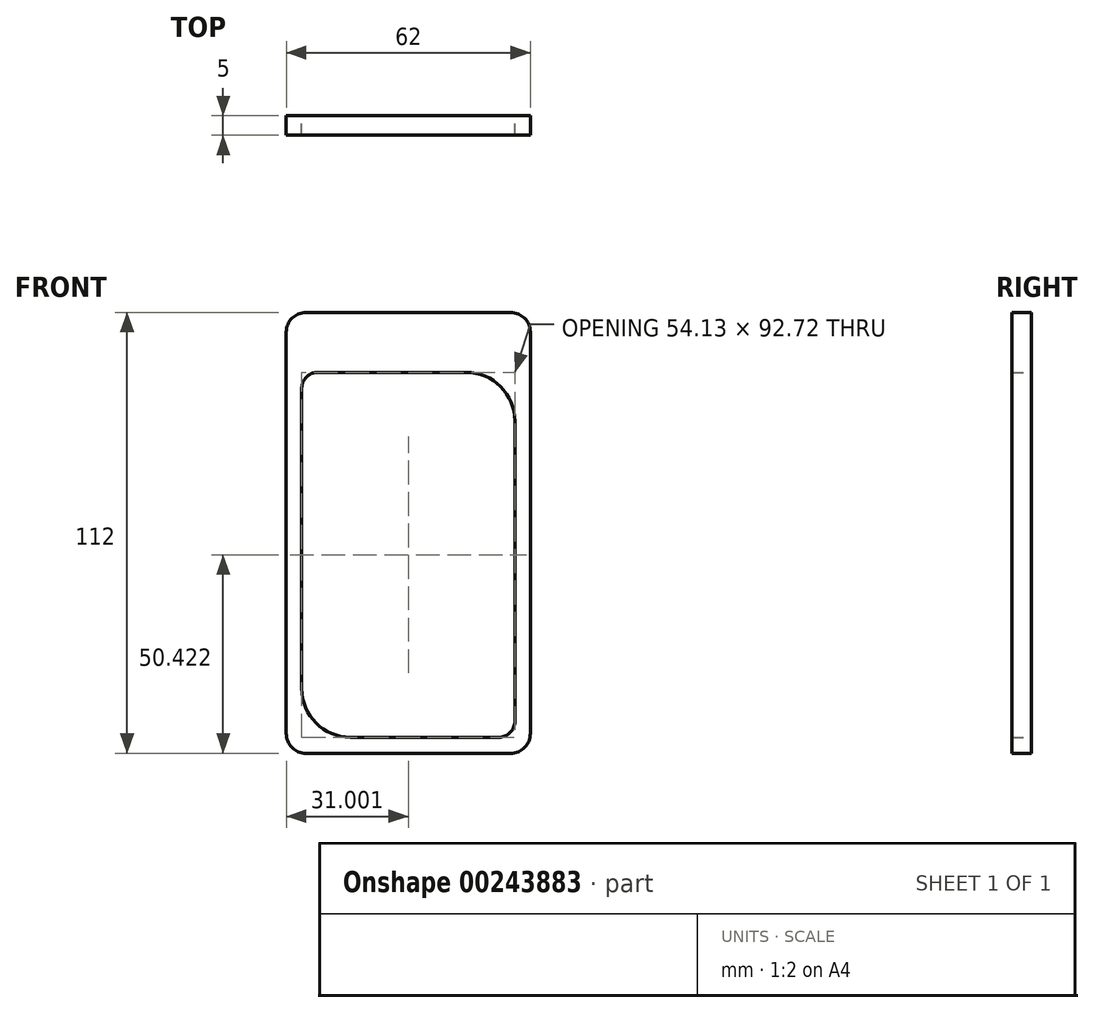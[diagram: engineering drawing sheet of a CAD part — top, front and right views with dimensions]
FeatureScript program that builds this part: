
annotation { "Feature Type Name" : "Feature", "Feature Type Description" : "" }
export const myFeature = defineFeature(function(context is Context, id is Id, definition is map)
    precondition{}
    {
        {
            var Q0;
            Q0=qCreatedBy(makeId("Front.planeOp"),FACE);
            var sketch = newSketch(context, id + "F0", { "sketchPlane" : qUnion([Q0])});
            skLineSegment(sketch, "E0.0", {"start": v(34.51, -44.26) * mm, "end": v(34.51, 32.04) * mm});
            skArc(sketch, "E0.1", {"start": v(26.45, -52.32) * mm, "mid": v(32.15, -49.96) * mm, "end": v(34.51, -44.26) * mm});
            skArc(sketch, "E0.4", {"start": v(-27.6, -35.96) * mm, "mid": v(-22.82, -47.53) * mm, "end": v(-11.25, -52.32) * mm});
            skLineSegment(sketch, "E0.5", {"start": v(-11.25, -52.32) * mm, "end": v(26.45, -52.32) * mm});
            skArc(sketch, "E1.0", {"start": v(18.15, 48.4) * mm, "mid": v(29.72, 43.61) * mm, "end": v(34.52, 32.04) * mm});
            skLineSegment(sketch, "E1.1", {"start": v(-19.55, 48.4) * mm, "end": v(18.15, 48.4) * mm});
            skLineSegment(sketch, "E2", {"start": v(-27.61, 40.34) * mm, "end": v(-27.6, -35.96) * mm});
            skArc(sketch, "E3", {"start": v(-19.55, 48.4) * mm, "mid": v(-25.25, 46.04) * mm, "end": v(-27.61, 40.34) * mm});
            skSolve(sketch);
        }
        {
            var Q0;
            Q0=qCreatedBy(makeId("Front.planeOp"),FACE);
            var sketch = newSketch(context, id + "F1", { "sketchPlane" : qUnion([Q0])});
            skLineSegment(sketch, "E4.bottom", {"start": v(34.45, -52.38) * mm, "end": v(-27.55, -52.38) * mm});
            skLineSegment(sketch, "E4.top", {"start": v(34.45, 59.62) * mm, "end": v(-27.55, 59.62) * mm});
            skLineSegment(sketch, "E4.left", {"start": v(34.45, -52.38) * mm, "end": v(34.45, 59.62) * mm});
            skLineSegment(sketch, "E4.right", {"start": v(-27.55, -52.38) * mm, "end": v(-27.55, 59.62) * mm});
            skSolve(sketch);
        }
        {
            var Q0;
            Q0=makeQuery(id+"F1.imprint","IMPRINT",FACE,{"disambiguationData":[TD([[makeQuery(id+"F1.imprint","IMPRINT",EDGE,{"derivedFrom":sQuery(id+"F1.wireOp",EDGE,"E4.bottom")}),-1.0]])]});
            extrude(context, id + "F2", {"entities" : qUnion([Q0]), "depth" : 5 * mm});
        }
        {
            var Q0;
            Q0=qCreatedBy(makeId("Front.planeOp"),FACE);
            var sketch = newSketch(context, id + "F3", { "sketchPlane" : qUnion([Q0])});
            skArc(sketch, "E5.0", {"start": v(18.15, 44.4) * mm, "mid": v(26.9, 40.78) * mm, "end": v(30.52, 32.04) * mm});
            skLineSegment(sketch, "E5.1", {"start": v(-19.55, 44.4) * mm, "end": v(18.15, 44.4) * mm});
            skArc(sketch, "E5.2", {"start": v(-19.55, 44.4) * mm, "mid": v(-22.42, 43.21) * mm, "end": v(-23.61, 40.34) * mm});
            skArc(sketch, "E5.3", {"start": v(26.45, -48.32) * mm, "mid": v(29.32, -47.13) * mm, "end": v(30.51, -44.26) * mm});
            skLineSegment(sketch, "E5.4", {"start": v(-11.25, -48.32) * mm, "end": v(26.45, -48.32) * mm});
            skArc(sketch, "E5.5", {"start": v(-23.6, -35.96) * mm, "mid": v(-19.99, -44.7) * mm, "end": v(-11.25, -48.32) * mm});
            skLineSegment(sketch, "E5.6", {"start": v(-23.61, 40.34) * mm, "end": v(-23.6, -35.96) * mm});
            skLineSegment(sketch, "E6", {"start": v(30.52, 32.04) * mm, "end": v(30.51, -44.26) * mm});
            skSolve(sketch);
        }
        {
            var Q0;
            Q0 = qSketchRegion(id + "F3", true);
            extrude(context, id + "F4", {"entities" : qUnion([Q0]), "operationType" : NewBodyOperationType.REMOVE, "depth" : 5 * mm});
        }
        {
            var Q0;
            Q0=makeQuery(id+"F2.opExtrude","SWEPT_EDGE",EDGE,{"disambiguationData":[OSD([sQuery(id+"F1.wireOp",EDGE,"E4.top"),sQuery(id+"F1.wireOp",EDGE,"E4.right")])]});
            var Q1;
            Q1=makeQuery(id+"F2.opExtrude","SWEPT_EDGE",EDGE,{"disambiguationData":[OSD([sQuery(id+"F1.wireOp",EDGE,"E4.bottom"),sQuery(id+"F1.wireOp",EDGE,"E4.right")])]});
            var Q2;
            Q2=makeQuery(id+"F2.opExtrude","SWEPT_EDGE",EDGE,{"disambiguationData":[OSD([sQuery(id+"F1.wireOp",EDGE,"E4.bottom"),sQuery(id+"F1.wireOp",EDGE,"E4.left")])]});
            var Q3;
            Q3=makeQuery(id+"F2.opExtrude","SWEPT_EDGE",EDGE,{"disambiguationData":[OSD([sQuery(id+"F1.wireOp",EDGE,"E4.top"),sQuery(id+"F1.wireOp",EDGE,"E4.left")])]});
            fillet(context, id + "F5", {"entities" : qUnion([Q0, Q1, Q2, Q3]), "radius" : 5 * mm, "tangentPropagation" : true, "allowEdgeOverflow" : false});
        }
    });
